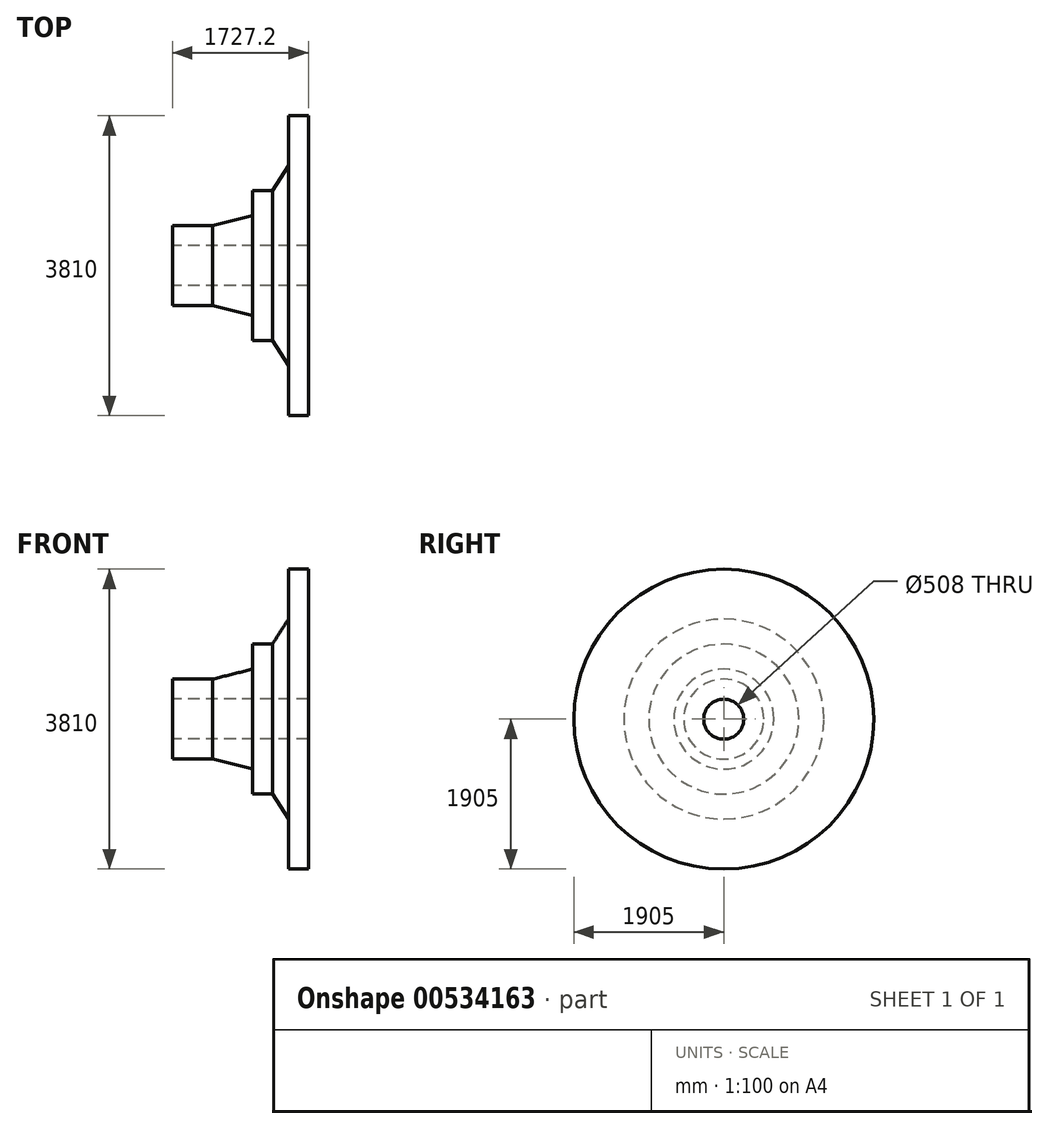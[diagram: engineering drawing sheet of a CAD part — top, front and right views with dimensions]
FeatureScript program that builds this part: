
annotation { "Feature Type Name" : "Feature", "Feature Type Description" : "" }
export const myFeature = defineFeature(function(context is Context, id is Id, definition is map)
    precondition{}
    {
        {
            var Q0;
            Q0=qCreatedBy(makeId("Front.planeOp"),FACE);
            var sketch = newSketch(context, id + "F0", { "sketchPlane" : qUnion([Q0])});
            skLineSegment(sketch, "E0", {"start": v(0.82, 254.49) * mm, "end": v(508.82, 254.49) * mm});
            skLineSegment(sketch, "E1", {"start": v(1016.82, 698.99) * mm, "end": v(1016.82, 381.49) * mm});
            skLineSegment(sketch, "E2", {"start": v(508.82, 254.49) * mm, "end": v(1016.82, 381.49) * mm});
            skLineSegment(sketch, "E3", {"start": v(0.82, 254.49) * mm, "end": v(0.82, 0.49) * mm});
            skLineSegment(sketch, "E4", {"start": v(1016.82, 698.99) * mm, "end": v(1270.82, 698.99) * mm});
            skLineSegment(sketch, "E5", {"start": v(0.82, 0.49) * mm, "end": v(1728.02, 0.49) * mm});
            skLineSegment(sketch, "E6", {"start": v(1728.02, 0.49) * mm, "end": v(1728.02, 1651.49) * mm});
            skLineSegment(sketch, "E7", {"start": v(1728.02, 1651.49) * mm, "end": v(1474.02, 1651.49) * mm});
            skLineSegment(sketch, "E8", {"start": v(1474.02, 1651.49) * mm, "end": v(1474.02, 1016.49) * mm});
            skLineSegment(sketch, "E9", {"start": v(1270.82, 698.99) * mm, "end": v(1474.02, 1016.49) * mm});
            skLineSegment(sketch, "E10", {"start": v(-431.34, -253.51) * mm, "end": v(2255.5, -253.51) * mm});
            skSolve(sketch);
        }
        {
            var Q0;
            Q0=makeQuery(id+"F0.imprint","IMPRINT",FACE,{"disambiguationData":[TD([[makeQuery(id+"F0.imprint","IMPRINT",EDGE,{"derivedFrom":sQuery(id+"F0.wireOp",EDGE,"E0")}),-1.0]])]});
            var Q1;
            Q1=sQuery(id+"F0.wireOp",EDGE,"E10");
            revolve(context, id + "F1", {"entities" : qUnion([Q0]), "axis" : qUnion([Q1]), "revolveType" : RevolveType.FULL});
        }
    });
